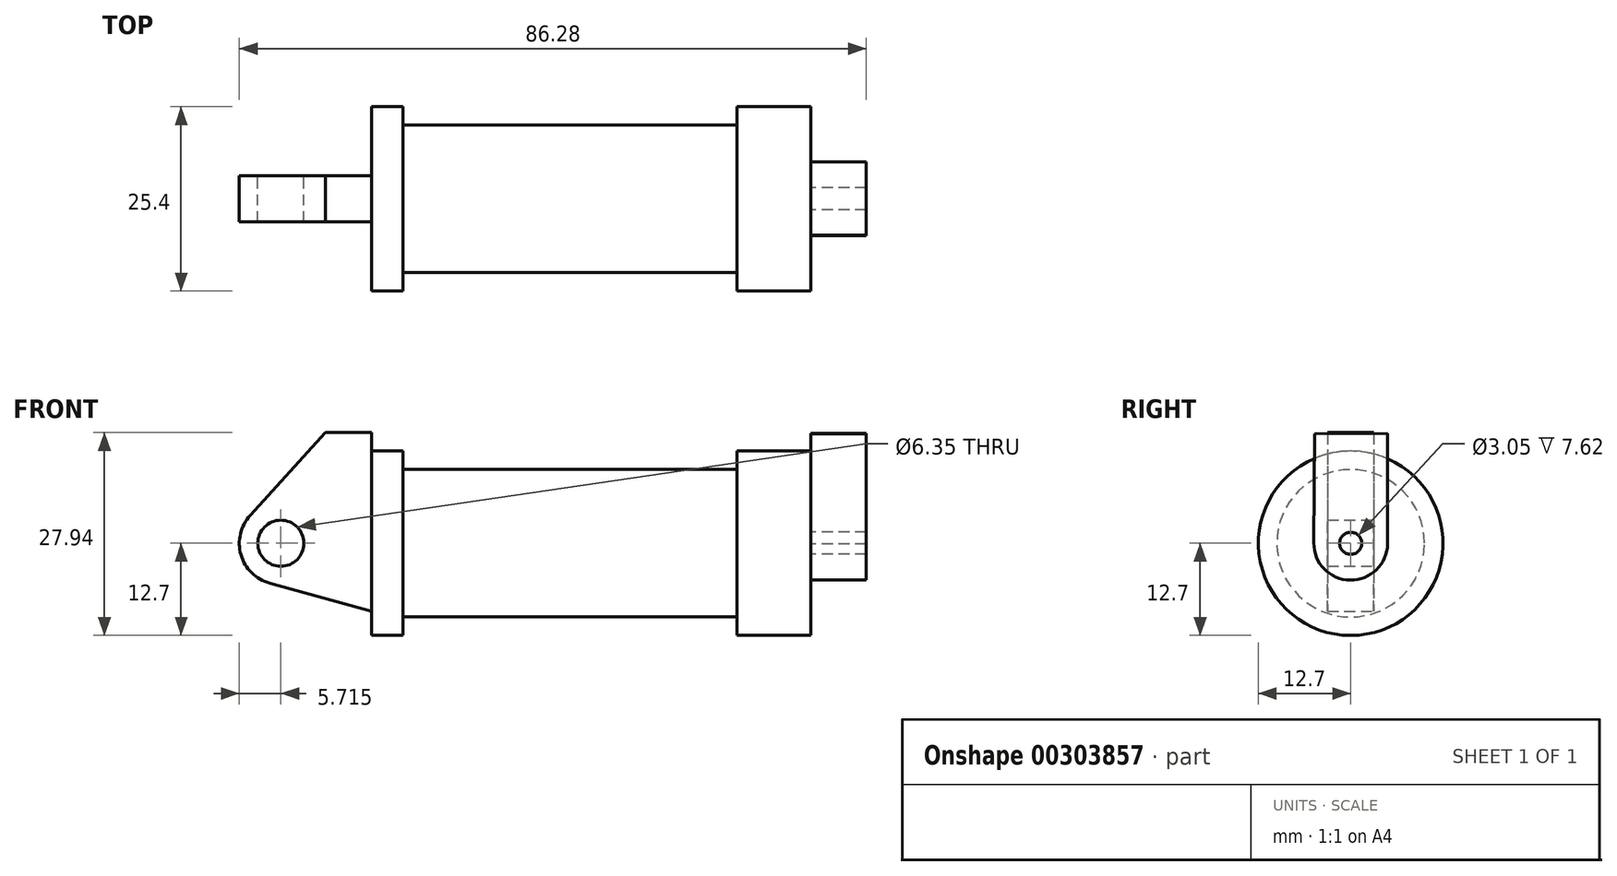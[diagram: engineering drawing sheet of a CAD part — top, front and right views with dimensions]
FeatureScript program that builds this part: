
annotation { "Feature Type Name" : "Feature", "Feature Type Description" : "" }
export const myFeature = defineFeature(function(context is Context, id is Id, definition is map)
    precondition{}
    {
        {
            var Q0;
            Q0=qCreatedBy(makeId("Front.planeOp"),FACE);
            var sketch = newSketch(context, id + "F0", { "sketchPlane" : qUnion([Q0])});
            skLineSegment(sketch, "E0", {"start": v(0, 0) * mm, "end": v(0, 12.7) * mm});
            skLineSegment(sketch, "E1", {"start": v(0, 12.7) * mm, "end": v(10.16, 12.7) * mm});
            skLineSegment(sketch, "E2", {"start": v(10.16, 12.7) * mm, "end": v(10.16, 10.16) * mm});
            skLineSegment(sketch, "E3", {"start": v(10.16, 10.16) * mm, "end": v(56.13, 10.16) * mm});
            skLineSegment(sketch, "E4", {"start": v(56.13, 10.16) * mm, "end": v(56.13, 12.7) * mm});
            skLineSegment(sketch, "E5", {"start": v(56.13, 12.7) * mm, "end": v(66.3, 12.7) * mm});
            skLineSegment(sketch, "E6", {"start": v(66.3, 12.7) * mm, "end": v(66.3, 0) * mm});
            skLineSegment(sketch, "E7", {"start": v(66.3, 0) * mm, "end": v(0, 0) * mm});
            skLineSegment(sketch, "E8", {"start": v(5.84, 15.24) * mm, "end": v(-0.5, 15.24) * mm});
            skLineSegment(sketch, "E9", {"start": v(-0.5, 15.24) * mm, "end": v(-10.88, 3.85) * mm});
            skLineSegment(sketch, "E10", {"start": v(0, 0) * mm, "end": v(-6.65, 0) * mm});
            skCircle(sketch, "E11", {"center": v(-6.65, 0) * mm, "radius": 5.72 * mm});
            skCircle(sketch, "E12", {"center": v(-6.65, 0) * mm, "radius": 3.18 * mm});
            skLineSegment(sketch, "E13", {"start": v(5.84, 15.24) * mm, "end": v(5.84, -9.4) * mm});
            skLineSegment(sketch, "E14", {"start": v(5.84, -9.4) * mm, "end": v(-8.18, -5.5) * mm});
            skSolve(sketch);
        }
        {
            var Q0;
            {var subQ0=sQuery(id+"F0.wireOp",EDGE,"E2");Q0=makeQuery(id+"F0.imprint","IMPRINT",FACE,{"disambiguationData":[TD([[makeQuery(id+"F0.imprint","IMPRINT",EDGE,{"derivedFrom":subQ0}),-1.0]])]});}
            var Q1;
            Q1=sQuery(id+"F0.wireOp",EDGE,"E7");
            revolve(context, id + "F1", {"entities" : qUnion([Q0]), "axis" : qUnion([Q1]), "revolveType" : RevolveType.FULL});
        }
        {
            var Q0;
            {var subQ0=sQuery(id+"F0.wireOp",EDGE,"E0");Q0=makeQuery(id+"F0.imprint","IMPRINT",FACE,{"disambiguationData":[TD([[makeQuery(id+"F0.imprint","IMPRINT",EDGE,{"derivedFrom":subQ0}),-1.0]])]});}
            var Q1;
            {var subQ1=sQuery(id+"F0.wireOp",EDGE,"E0");Q1=makeQuery(id+"F0.imprint","IMPRINT",FACE,{"disambiguationData":[TD([[makeQuery(id+"F0.imprint","IMPRINT",EDGE,{"derivedFrom":subQ1}),1.0]])]});}
            var Q2;
            {var subQ5=sQuery(id+"F0.wireOp",EDGE,"E12");Q2=makeQuery(id+"F0.imprint","IMPRINT",FACE,{"disambiguationData":[TD([[makeQuery(id+"F0.imprint","IMPRINT",EDGE,{"derivedFrom":subQ5}),-1.0]])]});}
            var Q3;
            {var subQ0=sQuery(id+"F0.wireOp",EDGE,"E14");Q3=makeQuery(id+"F0.imprint","IMPRINT",FACE,{"disambiguationData":[TD([[makeQuery(id+"F0.imprint","IMPRINT",EDGE,{"derivedFrom":subQ0}),-1.0]])]});}
            extrude(context, id + "F2", {"entities" : qUnion([Q0, Q1, Q2, Q3]), "operationType" : NewBodyOperationType.ADD, "endBound" : BoundingType.SYMMETRIC, "depth" : 6.35 * mm});
        }
        {
            var Q0;
            Q0=makeQuery(id+"F1.opRevolve","SWEPT_FACE",FACE,{"disambiguationData":[OSD([sQuery(id+"F0.wireOp",EDGE,"E6")])]});
            var sketch = newSketch(context, id + "F3", { "sketchPlane" : qUnion([Q0])});
            skCircle(sketch, "E15", {"center": v(0, 0) * mm, "radius": 1.52 * mm});
            skCircle(sketch, "E16", {"center": v(0, 0) * mm, "radius": 5.08 * mm});
            skLineSegment(sketch, "E17", {"start": v(5.08, -0.08) * mm, "end": v(5.08, 15.16) * mm});
            skLineSegment(sketch, "E18", {"start": v(-4.97, 15.09) * mm, "end": v(-5.08, 0.04) * mm});
            skLineSegment(sketch, "E19", {"start": v(5.08, 15.16) * mm, "end": v(-4.97, 15.09) * mm});
            skSolve(sketch);
        }
        {
            var Q0;
            {var subQ0=sQuery(id+"F3.wireOp",EDGE,"E18");var subQ1=sQuery(id+"F3.wireOp",EDGE,"E16");var subQ2=makeQuery(id+"F3.imprint","INTERSECT",VERTEX,{"derivedFrom":[subQ1,subQ0]});Q0=makeQuery(id+"F3.imprint","IMPRINT",FACE,{"disambiguationData":[TD([[makeQuery(id+"F3.imprint","IMPRINT",EDGE,{"disambiguationData":[TD([[subQ2,1.0]])],"derivedFrom":subQ1}),-1.0]])]});}
            var Q1;
            Q1=makeQuery(id+"F3.imprint","IMPRINT",FACE,{"disambiguationData":[TD([[makeQuery(id+"F3.imprint","IMPRINT",EDGE,{"derivedFrom":sQuery(id+"F3.wireOp",EDGE,"E15")}),-1.0]])]});
            var Q2;
            {var subQ0=sQuery(id+"F3.wireOp",EDGE,"E19");Q2=makeQuery(id+"F3.imprint","IMPRINT",FACE,{"disambiguationData":[TD([[makeQuery(id+"F3.imprint","IMPRINT",EDGE,{"derivedFrom":subQ0}),1.0]])]});}
            extrude(context, id + "F4", {"entities" : qUnion([Q0, Q1, Q2]), "operationType" : NewBodyOperationType.ADD, "depth" : 7.62 * mm});
        }
    });
